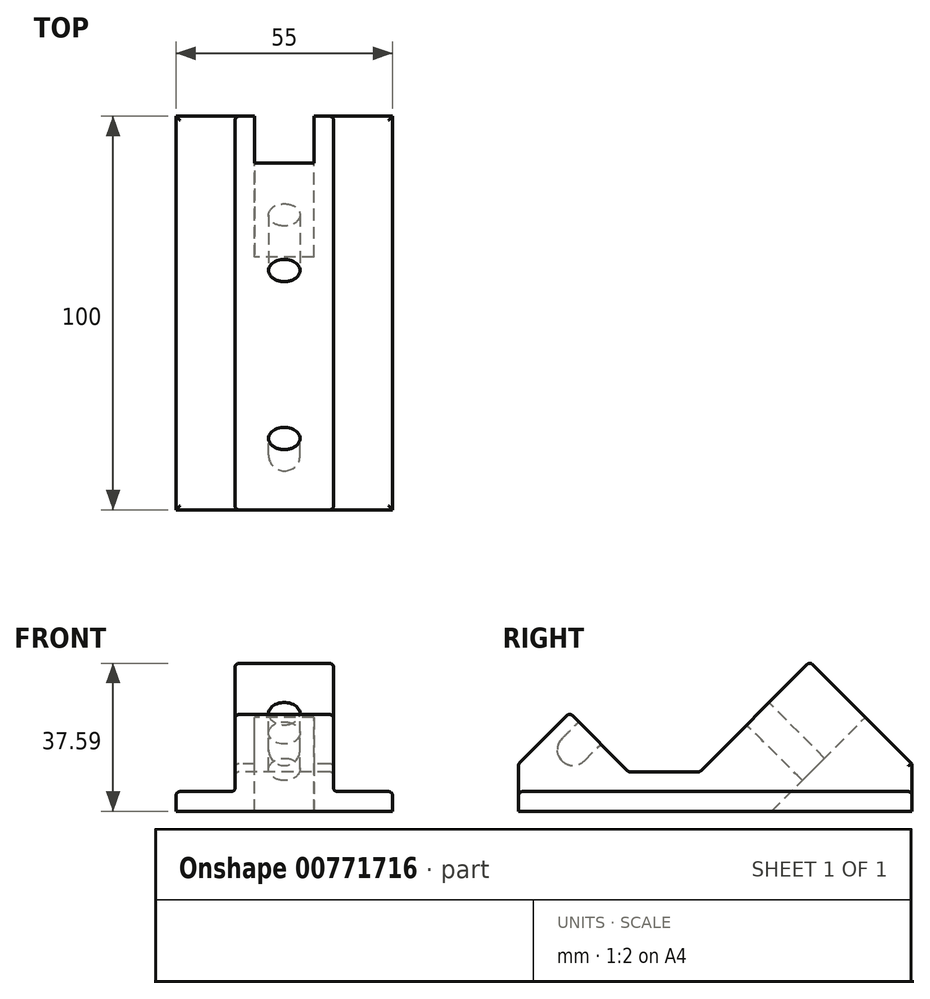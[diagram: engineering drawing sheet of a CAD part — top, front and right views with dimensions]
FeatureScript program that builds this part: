
annotation { "Feature Type Name" : "Feature", "Feature Type Description" : "" }
export const myFeature = defineFeature(function(context is Context, id is Id, definition is map)
    precondition{}
    {
        {
            var Q0;
            Q0=qCreatedBy(makeId("Top.planeOp"),FACE);
            var sketch = newSketch(context, id + "F0", { "sketchPlane" : qUnion([Q0])});
            skLineSegment(sketch, "E0.bottom", {"start": v(-23.35, 60.49) * mm, "end": v(31.65, 60.49) * mm});
            skLineSegment(sketch, "E0.top", {"start": v(-23.35, -39.51) * mm, "end": v(31.65, -39.51) * mm});
            skLineSegment(sketch, "E0.left", {"start": v(-23.35, 60.49) * mm, "end": v(-23.35, -39.51) * mm});
            skLineSegment(sketch, "E0.right", {"start": v(31.65, 60.49) * mm, "end": v(31.65, -39.51) * mm});
            skSolve(sketch);
        }
        {
            var Q0;
            Q0=makeQuery(id+"F0.imprint","IMPRINT",FACE,{"disambiguationData":[TD([[makeQuery(id+"F0.imprint","IMPRINT",EDGE,{"derivedFrom":sQuery(id+"F0.wireOp",EDGE,"E0.bottom")}),-1.0]])]});
            extrude(context, id + "F1", {"entities" : qUnion([Q0]), "depth" : 5 * mm, "offsetDistance" : 25 * mm});
        }
        {
            var Q0;
            Q0=makeQuery(id+"F1.opExtrude","CAP_FACE",FACE,{"disambiguationData":[OSD([sQuery(id+"F0.wireOp",EDGE,"E0.bottom"),sQuery(id+"F0.wireOp",EDGE,"E0.top"),sQuery(id+"F0.wireOp",EDGE,"E0.left"),sQuery(id+"F0.wireOp",EDGE,"E0.right")])],"isStart":false});
            var sketch = newSketch(context, id + "F2", { "sketchPlane" : qUnion([Q0])});
            skLineSegment(sketch, "E1.bottom", {"start": v(16.65, 60.49) * mm, "end": v(-8.35, 60.49) * mm});
            skLineSegment(sketch, "E1.top", {"start": v(16.65, -39.51) * mm, "end": v(-8.35, -39.51) * mm});
            skLineSegment(sketch, "E1.left", {"start": v(16.65, 60.49) * mm, "end": v(16.65, -39.51) * mm});
            skLineSegment(sketch, "E1.right", {"start": v(-8.35, 60.49) * mm, "end": v(-8.35, -39.51) * mm});
            skPoint(sketch, "E1.middle", {"position": v(4.15, 10.49) * mm});
            skPoint(sketch, "E1.middle.positionSnap0", {"position": v(31.65, 10.49) * mm});
            skPoint(sketch, "E1.middle.positionSnap1", {"position": v(4.15, 60.49) * mm});
            skPoint(sketch, "E1.centerSnap0", {"position": v(31.65, 10.49) * mm});
            skPoint(sketch, "E1.centerSnap1", {"position": v(4.15, 60.49) * mm});
            skSolve(sketch);
        }
        {
            var Q0;
            Q0=makeQuery(id+"F2.imprint","IMPRINT",FACE,{"disambiguationData":[TD([[makeQuery(id+"F2.imprint","IMPRINT",EDGE,{"derivedFrom":sQuery(id+"F2.wireOp",EDGE,"E1.bottom")}),-1.0]])]});
            extrude(context, id + "F3", {"entities" : qUnion([Q0]), "operationType" : NewBodyOperationType.ADD, "endBound" : BoundingType.THROUGH_ALL, "depth" : 40 * mm, "offsetDistance" : 25 * mm});
        }
        {
            var Q0;
            Q0=makeQuery(id+"F3.opExtrude","SWEPT_FACE",FACE,{"disambiguationData":[OSD([sQuery(id+"F2.wireOp",EDGE,"E1.right")])]});
            var sketch = newSketch(context, id + "F4", { "sketchPlane" : qUnion([Q0])});
            skLineSegment(sketch, "E2", {"start": v(-60.49, 12) * mm, "end": v(-34.49, 38) * mm});
            skLineSegment(sketch, "E3", {"start": v(-34.49, 38) * mm, "end": v(-6.49, 10) * mm});
            skLineSegment(sketch, "E4", {"start": v(-6.49, 10) * mm, "end": v(11.51, 10) * mm});
            skLineSegment(sketch, "E5", {"start": v(11.51, 10) * mm, "end": v(26.51, 25) * mm});
            skLineSegment(sketch, "E6", {"start": v(26.51, 25) * mm, "end": v(39.51, 12) * mm});
            skLineSegment(sketch, "E7", {"start": v(-60.49, 12) * mm, "end": v(-60.49, 5) * mm});
            skLineSegment(sketch, "E8", {"start": v(-60.49, 5) * mm, "end": v(39.51, 5) * mm});
            skLineSegment(sketch, "E9", {"start": v(39.51, 5) * mm, "end": v(39.51, 12) * mm});
            skSolve(sketch);
        }
        {
            var Q0;
            {var subQ1=sQuery(id+"F4.wireOp",EDGE,"E3");Q0=makeQuery(id+"F4.imprint","IMPRINT",FACE,{"disambiguationData":[TD([[makeQuery(id+"F4.imprint","IMPRINT",EDGE,{"derivedFrom":subQ1}),1.0]])]});}
            var Q1;
            {var subQ0=sQuery(id+"F4.wireOp",EDGE,"E2");Q1=makeQuery(id+"F4.imprint","IMPRINT",FACE,{"disambiguationData":[TD([[makeQuery(id+"F4.imprint","IMPRINT",EDGE,{"derivedFrom":subQ0}),1.0]])]});}
            extrude(context, id + "F5", {"entities" : qUnion([Q0, Q1]), "operationType" : NewBodyOperationType.REMOVE, "endBound" : BoundingType.THROUGH_ALL, "oppositeDirection" : true, "depth" : 25 * mm, "offsetDistance" : 25 * mm});
        }
        {
            var Q0;
            Q0=makeQuery(id+"F5.boolean.opBoolean","COPY",FACE,{"derivedFrom":makeQuery(id+"F5.opExtrude","SWEPT_FACE",FACE,{"disambiguationData":[OSD([sQuery(id+"F4.wireOp",EDGE,"E5")])]})});
            var sketch = newSketch(context, id + "F6", { "sketchPlane" : qUnion([Q0])});
            skLineSegment(sketch, "E10", {"start": v(-4.15, 36.43) * mm, "end": v(-4.15, 29.18) * mm, "construction": true});
            skCircle(sketch, "E11", {"center": v(-4.15, 29.18) * mm, "radius": 4 * mm});
            skSolve(sketch);
        }
        {
            var Q0;
            Q0=makeQuery(id+"F6.imprint","IMPRINT",FACE,{"disambiguationData":[TD([[makeQuery(id+"F6.imprint","IMPRINT",EDGE,{"derivedFrom":sQuery(id+"F6.wireOp",EDGE,"E11")}),1.0]])]});
            extrude(context, id + "F7", {"entities" : qUnion([Q0]), "operationType" : NewBodyOperationType.REMOVE, "oppositeDirection" : true, "depth" : 10 * mm, "offsetDistance" : 25 * mm});
        }
        {
            var Q0;
            Q0=makeQuery(id+"F5.boolean.opBoolean","COPY",FACE,{"derivedFrom":makeQuery(id+"F5.opExtrude","SWEPT_FACE",FACE,{"disambiguationData":[OSD([sQuery(id+"F4.wireOp",EDGE,"E3")])]})});
            var sketch = newSketch(context, id + "F8", { "sketchPlane" : qUnion([Q0])});
            skLineSegment(sketch, "E12", {"start": v(4.15, 51.26) * mm, "end": v(4.15, 32.6) * mm, "construction": true});
            skSolve(sketch);
        }
        {
            var Q0;
            Q0=sQuery(id+"F8.wireOp",VERTEX,"E12.end");
            var Q1;
            Q1=makeQuery(id+"F1.opExtrude","SWEPT_BODY",BODY,{"disambiguationData":[OSD([sQuery(id+"F0.wireOp",EDGE,"E0.bottom"),sQuery(id+"F0.wireOp",EDGE,"E0.top"),sQuery(id+"F0.wireOp",EDGE,"E0.left"),sQuery(id+"F0.wireOp",EDGE,"E0.right")])]});
            hole(context, id + "F9", {"style" : HoleStyle.SIMPLE, "endStyle" : HoleEndStyle.THROUGH, "holeDiameter" : 8 * mm, "majorDiameter" : 5 * mm, "isTappedThrough" : true, "tappedDepth" : 12 * mm, "tapClearance" : 3, "locations" : qUnion([Q0]), "scope" : qUnion([Q1])});
        }
        {
            var Q0;
            Q0=makeQuery(id+"F5.boolean.opBoolean","COPY",FACE,{"derivedFrom":makeQuery(id+"F5.opExtrude","SWEPT_FACE",FACE,{"disambiguationData":[OSD([sQuery(id+"F4.wireOp",EDGE,"E2")])]})});
            var sketch = newSketch(context, id + "F10", { "sketchPlane" : qUnion([Q0])});
            skLineSegment(sketch, "E13", {"start": v(-4.15, 2.48) * mm, "end": v(-4.15, -17.52) * mm, "construction": true});
            skLineSegment(sketch, "E14", {"start": v(-11.65, -17.52) * mm, "end": v(3.35, -17.52) * mm});
            skPoint(sketch, "E14.startSnap0", {"position": v(8.35, -17.52) * mm});
            skLineSegment(sketch, "E15", {"start": v(-11.65, -17.52) * mm, "end": v(-11.65, -63.18) * mm});
            skLineSegment(sketch, "E16", {"start": v(-11.65, -63.18) * mm, "end": v(3.35, -63.18) * mm});
            skLineSegment(sketch, "E17", {"start": v(3.35, -63.18) * mm, "end": v(3.35, -17.52) * mm});
            skSolve(sketch);
        }
        {
            var Q0;
            {var subQ0=sQuery(id+"F10.wireOp",EDGE,"E16");Q0=makeQuery(id+"F10.imprint","IMPRINT",FACE,{"disambiguationData":[TD([[makeQuery(id+"F10.imprint","IMPRINT",EDGE,{"derivedFrom":subQ0}),1.0]])]});}
            var Q1;
            {var subQ0=sQuery(id+"F10.wireOp",EDGE,"E14");Q1=makeQuery(id+"F10.imprint","IMPRINT",FACE,{"disambiguationData":[TD([[makeQuery(id+"F10.imprint","IMPRINT",EDGE,{"derivedFrom":subQ0}),-1.0]])]});}
            var Q2;
            Q2=sQuery(id+"F10.wireOp",EDGE,"gWLXlSv5-rtWf-nAGO-u5nC-w5gl4VhghfOW");
            var Q3;
            Q3=sQuery(id+"F10.wireOp",EDGE,"6AZvcZhi-jqI9-GNc7-rUj6-xlDhPe7SM3Dv");
            var Q4;
            Q4=sQuery(id+"F10.wireOp",EDGE,"UAXWCAyl-5tks-AbJN-HeVI-GcQKpSMmbsgf");
            extrude(context, id + "F11", {"entities" : qUnion([Q0, Q1]), "operationType" : NewBodyOperationType.REMOVE, "surfaceEntities" : qUnion([Q2, Q3, Q4]), "endBound" : BoundingType.THROUGH_ALL, "oppositeDirection" : true, "depth" : 25 * mm, "offsetDistance" : 25 * mm});
        }
        {
            var Q0;
            Q0=makeQuery(id+"F7.boolean.opBoolean","COPY",FACE,{"derivedFrom":makeQuery(id+"F7.opExtrude","CAP_FACE",FACE,{"disambiguationData":[OSD([sQuery(id+"F6.wireOp",EDGE,"E11")])],"isStart":false})});
            fillet(context, id + "F12", {"entities" : qUnion([Q0]), "radius" : 4 * mm, "allowEdgeOverflow" : false});
        }
        {
            var Q0;
            Q0=makeQuery(id+"F3.opExtrude","SWEPT_FACE",FACE,{"disambiguationData":[OSD([sQuery(id+"F2.wireOp",EDGE,"E1.right")])]});
            var Q1;
            Q1=makeQuery(id+"F3.opExtrude","SWEPT_FACE",FACE,{"disambiguationData":[OSD([sQuery(id+"F2.wireOp",EDGE,"E1.left")])]});
            var Q2;
            {var subQ0=sQuery(id+"F0.wireOp",EDGE,"E0.top");var subQ1=sQuery(id+"F0.wireOp",EDGE,"E0.right");var subQ2=sQuery(id+"F0.wireOp",EDGE,"E0.bottom");Q2=makeQuery(id+"F3.boolean.opBoolean","SPLIT",FACE,{"disambiguationData":[TD([makeQuery(id+"F1.opExtrude","SWEPT_FACE",FACE,{"disambiguationData":[OSD([subQ1])]})])],"derivedFrom":makeQuery(id+"F1.opExtrude","CAP_FACE",FACE,{"disambiguationData":[OSD([subQ2,subQ0,sQuery(id+"F0.wireOp",EDGE,"E0.left"),subQ1])],"isStart":false})});}
            var Q3;
            {var subQ0=sQuery(id+"F0.wireOp",EDGE,"E0.left");var subQ1=sQuery(id+"F0.wireOp",EDGE,"E0.top");var subQ2=sQuery(id+"F0.wireOp",EDGE,"E0.bottom");Q3=makeQuery(id+"F3.boolean.opBoolean","SPLIT",FACE,{"disambiguationData":[TD([makeQuery(id+"F1.opExtrude","SWEPT_FACE",FACE,{"disambiguationData":[OSD([subQ0])]})])],"derivedFrom":makeQuery(id+"F1.opExtrude","CAP_FACE",FACE,{"disambiguationData":[OSD([subQ2,subQ1,subQ0,sQuery(id+"F0.wireOp",EDGE,"E0.right")])],"isStart":false})});}
            var Q4;
            Q4=makeQuery(id+"F5.boolean.opBoolean","COPY",FACE,{"derivedFrom":makeQuery(id+"F5.opExtrude","SWEPT_FACE",FACE,{"disambiguationData":[OSD([sQuery(id+"F4.wireOp",EDGE,"E4")])]})});
            var Q5;
            Q5=makeQuery(id+"F5.boolean.opBoolean","COPY",FACE,{"derivedFrom":makeQuery(id+"F5.opExtrude","SWEPT_FACE",FACE,{"disambiguationData":[OSD([sQuery(id+"F4.wireOp",EDGE,"E6")])]})});
            var Q6;
            Q6=makeQuery(id+"F9.hole-0.boolean.opBoolean","COPY",EDGE,{"derivedFrom":makeQuery(id+"F9.hole-0.opRevolve","SWEPT_EDGE",EDGE,{"disambiguationData":[OSD([sQuery(id+"F9.hole-0.sketch.wireOp",EDGE,"core_line_2"),sQuery(id+"F9.hole-0.sketch.wireOp",EDGE,"core_line_3")])]})});
            var Q7;
            Q7=makeQuery(id+"F5.boolean.opBoolean","COPY",EDGE,{"derivedFrom":makeQuery(id+"F5.opExtrude","SWEPT_EDGE",EDGE,{"disambiguationData":[OSD([sQuery(id+"F4.wireOp",EDGE,"E2"),sQuery(id+"F4.wireOp",EDGE,"E3")])]})});
            fillet(context, id + "F13", {"entities" : qUnion([Q0, Q1, Q2, Q3, Q4, Q5, Q6, Q7]), "radius" : 1 * mm, "tangentPropagation" : true, "allowEdgeOverflow" : false});
        }
    });
